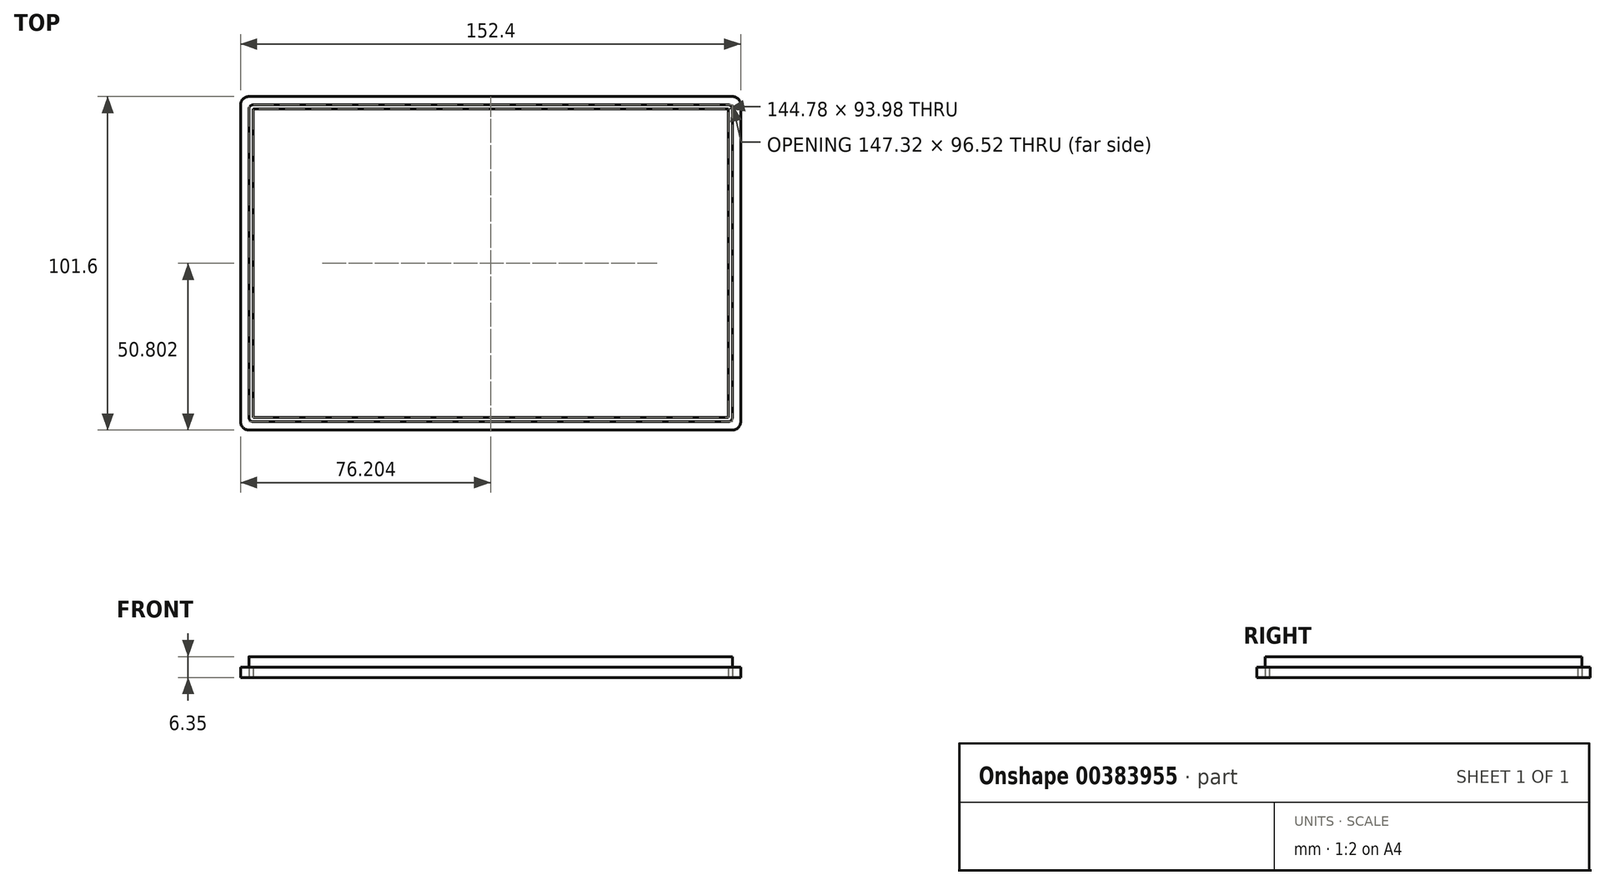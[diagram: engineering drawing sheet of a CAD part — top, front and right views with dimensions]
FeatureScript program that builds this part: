
annotation { "Feature Type Name" : "Feature", "Feature Type Description" : "" }
export const myFeature = defineFeature(function(context is Context, id is Id, definition is map)
    precondition{}
    {
        {
            var Q0;
            Q0=qCreatedBy(makeId("Top.planeOp"),FACE);
            var sketch = newSketch(context, id + "F0", { "sketchPlane" : qUnion([Q0])});
            skLineSegment(sketch, "E0.bottom", {"start": v(-77.99, 47.6) * mm, "end": v(69.33, 47.6) * mm});
            skLineSegment(sketch, "E0.top", {"start": v(-77.99, -54) * mm, "end": v(69.33, -54) * mm});
            skLineSegment(sketch, "E0.left", {"start": v(-80.53, 45.05) * mm, "end": v(-80.53, -51.47) * mm});
            skLineSegment(sketch, "E0.right", {"start": v(71.87, 45.05) * mm, "end": v(71.87, -51.47) * mm});
            skPoint(sketch, "E1.visualSharp", {"position": v(-80.53, 47.6) * mm});
            skArc(sketch, "E1.filletArc", {"start": v(-77.99, 47.6) * mm, "mid": v(-79.78, 46.85) * mm, "end": v(-80.53, 45.05) * mm});
            skPoint(sketch, "E2.visualSharp", {"position": v(71.87, 47.6) * mm});
            skArc(sketch, "E2.filletArc", {"start": v(71.87, 45.05) * mm, "mid": v(71.13, 46.85) * mm, "end": v(69.33, 47.6) * mm});
            skPoint(sketch, "E3.visualSharp", {"position": v(-80.53, -54) * mm});
            skArc(sketch, "E3.filletArc", {"start": v(-80.53, -51.47) * mm, "mid": v(-79.78, -53.26) * mm, "end": v(-77.99, -54) * mm});
            skPoint(sketch, "E4.visualSharp", {"position": v(71.87, -54) * mm});
            skArc(sketch, "E4.filletArc", {"start": v(69.33, -54) * mm, "mid": v(71.13, -53.26) * mm, "end": v(71.87, -51.47) * mm});
            skLineSegment(sketch, "E5.bottom", {"start": v(-76.72, 45.05) * mm, "end": v(68.06, 45.05) * mm});
            skLineSegment(sketch, "E5.top", {"start": v(-76.72, -51.47) * mm, "end": v(68.06, -51.47) * mm});
            skLineSegment(sketch, "E5.left", {"start": v(-77.99, 43.78) * mm, "end": v(-77.99, -50.2) * mm});
            skLineSegment(sketch, "E5.right", {"start": v(69.33, 43.78) * mm, "end": v(69.33, -50.2) * mm});
            skArc(sketch, "E6.filletArc", {"start": v(-76.72, 45.05) * mm, "mid": v(-77.61, 44.68) * mm, "end": v(-77.99, 43.78) * mm});
            skArc(sketch, "E7.filletArc", {"start": v(-77.99, -50.2) * mm, "mid": v(-77.61, -51.1) * mm, "end": v(-76.72, -51.47) * mm});
            skArc(sketch, "E8.filletArc", {"start": v(68.06, -51.47) * mm, "mid": v(68.96, -51.1) * mm, "end": v(69.33, -50.2) * mm});
            skArc(sketch, "E9.filletArc", {"start": v(69.33, 43.78) * mm, "mid": v(68.96, 44.68) * mm, "end": v(68.06, 45.05) * mm});
            skLineSegment(sketch, "E10.bottom", {"start": v(-76.72, 43.78) * mm, "end": v(68.06, 43.78) * mm});
            skLineSegment(sketch, "E10.top", {"start": v(-76.72, -50.2) * mm, "end": v(68.06, -50.2) * mm});
            skLineSegment(sketch, "E10.left", {"start": v(-76.72, 43.78) * mm, "end": v(-76.72, -50.2) * mm});
            skLineSegment(sketch, "E10.right", {"start": v(68.06, 43.78) * mm, "end": v(68.06, -50.2) * mm});
            skSolve(sketch);
        }
        {
            var Q0;
            Q0=makeQuery(id+"F0.imprint","IMPRINT",FACE,{"disambiguationData":[TD([[makeQuery(id+"F0.imprint","IMPRINT",EDGE,{"derivedFrom":sQuery(id+"F0.wireOp",EDGE,"E0.bottom")}),-1.0]])]});
            var Q1;
            Q1=makeQuery(id+"F0.imprint","IMPRINT",FACE,{"disambiguationData":[TD([[makeQuery(id+"F0.imprint","IMPRINT",EDGE,{"derivedFrom":sQuery(id+"F0.wireOp",EDGE,"E10.bottom")}),-1.0]])]});
            extrude(context, id + "F1", {"entities" : qUnion([Q0, Q1]), "depth" : 3.17 * mm});
        }
        {
            var Q0;
            Q0=makeQuery(id+"F0.imprint","IMPRINT",FACE,{"disambiguationData":[TD([[makeQuery(id+"F0.imprint","IMPRINT",EDGE,{"derivedFrom":sQuery(id+"F0.wireOp",EDGE,"E5.bottom")}),-1.0]])]});
            extrude(context, id + "F2", {"entities" : qUnion([Q0]), "depth" : 6.35 * mm});
        }
    });
